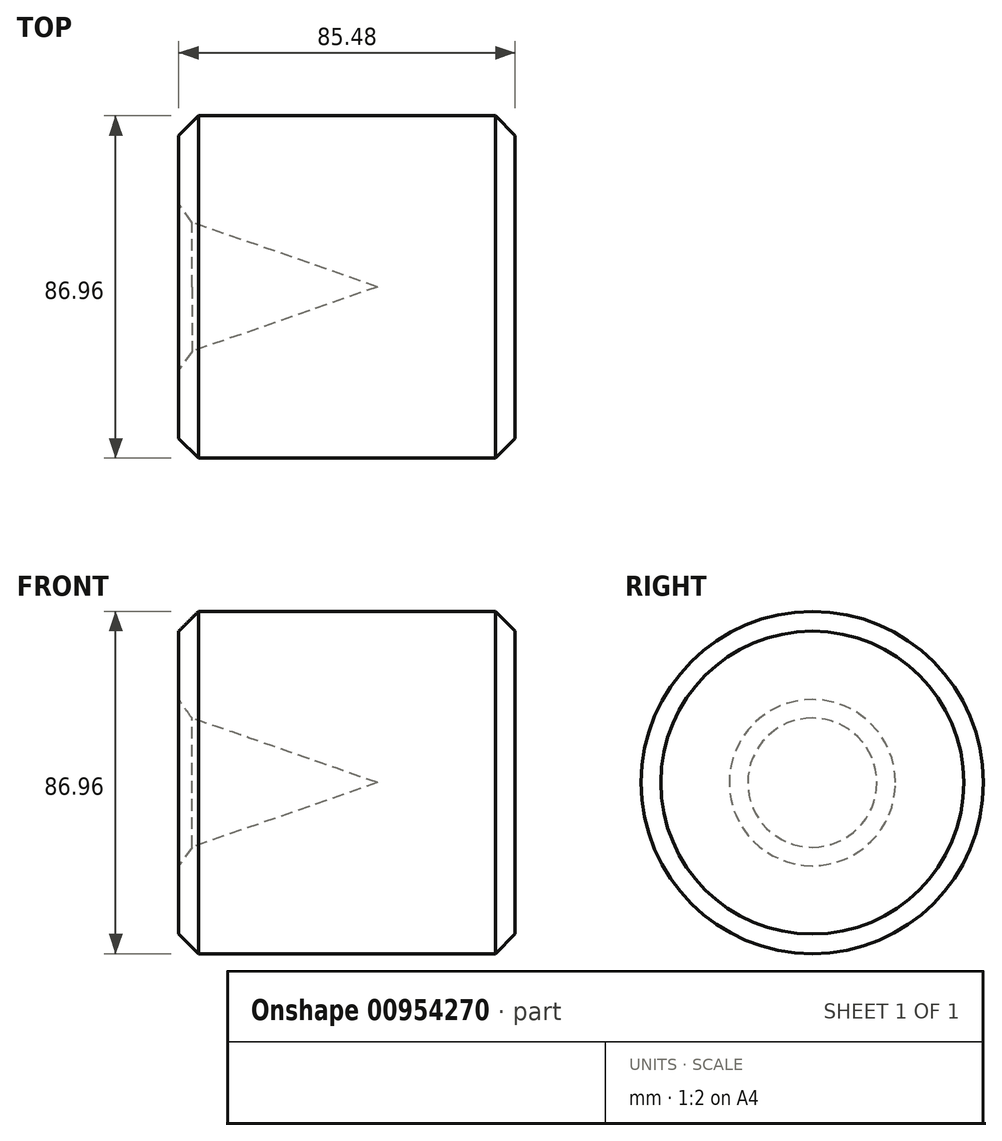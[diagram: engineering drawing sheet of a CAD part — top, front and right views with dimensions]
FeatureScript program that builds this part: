
annotation { "Feature Type Name" : "Feature", "Feature Type Description" : "" }
export const myFeature = defineFeature(function(context is Context, id is Id, definition is map)
    precondition{}
    {
        {
            var Q0;
            Q0=qCreatedBy(makeId("Front.planeOp"),FACE);
            var sketch = newSketch(context, id + "F0", { "sketchPlane" : qUnion([Q0])});
            skLineSegment(sketch, "E0", {"start": v(-50.56, 43.48) * mm, "end": v(34.92, 43.48) * mm});
            skLineSegment(sketch, "E1", {"start": v(34.92, 43.48) * mm, "end": v(34.92, 17.56) * mm});
            skLineSegment(sketch, "E2", {"start": v(34.92, 17.56) * mm, "end": v(34.92, 0) * mm});
            skLineSegment(sketch, "E3", {"start": v(34.92, 0) * mm, "end": v(0, 0) * mm});
            skLineSegment(sketch, "E4", {"start": v(-50.56, 43.48) * mm, "end": v(-50.56, 17.56) * mm});
            skLineSegment(sketch, "E5", {"start": v(-50.56, 17.56) * mm, "end": v(0, 0) * mm});
            skSolve(sketch);
        }
        {
            var Q0;
            Q0=makeQuery(id+"F0.imprint","IMPRINT",FACE,{"disambiguationData":[TD([[makeQuery(id+"F0.imprint","IMPRINT",EDGE,{"derivedFrom":sQuery(id+"F0.wireOp",EDGE,"E0")}),-1.0]])]});
            var Q1;
            Q1=sQuery(id+"F0.wireOp",EDGE,"E3");
            revolve(context, id + "F1", {"surfaceOperationType" : NewSurfaceOperationType.NEW, "entities" : qUnion([Q0]), "axis" : qUnion([Q1]), "revolveType" : RevolveType.FULL});
        }
        {
            var Q0;
            Q0=makeQuery(id+"F1.opRevolve","SWEPT_EDGE",EDGE,{"disambiguationData":[OSD([sQuery(id+"F0.wireOp",EDGE,"E0"),sQuery(id+"F0.wireOp",EDGE,"E4")])]});
            chamfer(context, id + "F2", {"entities" : qUnion([Q0]), "width" : 5 * mm, "tangentPropagation" : true});
        }
        {
            var Q0;
            Q0=makeQuery(id+"F1.opRevolve","SWEPT_EDGE",EDGE,{"disambiguationData":[OSD([sQuery(id+"F0.wireOp",EDGE,"E4"),sQuery(id+"F0.wireOp",EDGE,"E5")])]});
            chamfer(context, id + "F3", {"entities" : qUnion([Q0]), "width" : 5 * mm, "tangentPropagation" : true});
        }
        {
            var Q0;
            Q0=makeQuery(id+"F1.opRevolve","SWEPT_EDGE",EDGE,{"disambiguationData":[OSD([sQuery(id+"F0.wireOp",EDGE,"E0"),sQuery(id+"F0.wireOp",EDGE,"E1")])]});
            chamfer(context, id + "F4", {"entities" : qUnion([Q0]), "width" : 5 * mm, "tangentPropagation" : true});
        }
    });
